# Revit family: xNBS_Bobrick_BackRest_B-5892
name_source: partatom
category: Furniture
revit_build: Autodesk Revit 2015 (Build: 20140606_1530(x64)
units: mm (PartAtom-declared; Revit-internal decimal feet)

## types (1)
- B-5892
    Assembly Code = C1030200
    AssetType = Fixed
    BIMObjectName = Bobrick_WCBackrests_B-5892
    BackRestDepth = 36 mm  [stored 0.11811 ft]
    BackRestMaterial = Foam-Bobrick-Polyurethane White
    BackRestWidth = 360 mm  [stored 1.1811 ft]
    Category = Pr_40_20_76_98:WC pan backrests
    Cost = 0 $
    Default Elevation = 680 mm  [stored 2.23097 ft]
    Depth = 242 mm  [stored 0.793963 ft]
    Description = 32mm (1-1⁄4") Diameter Stainless Steel Grab Bar with Padded Back Rest
    DurationUnit = year
    GrabBarRadius = 16 mm  [stored 0.0524934 ft]
    GrabRailMaterial = Stainless Steel-Bobrick-Type 308-18 Gauge-Satin
    Height = 32 mm  [stored 0.104987 ft]
    IfcExportAs = IfcFurnitureType
    IfcExportType = USERDEFINED
    Manufacturer = Bobrick Washroom Equipment Ltd.
    ManufacturerURL = http://www.bobrick.co.uk
    Model = B-5892
    ModelReference = WC Backrest
    NBSCertification = http://www.nationalbimlibrary.com
    NBSDescription = WC backrests
    NBSReference = 45-35-72/382
    Name = B-5892
    NominalDepth = 281 mm  [stored 0.921916 ft]
    NominalHeight = 160 mm  [stored 0.524934 ft]
    NominalLength = 405 mm
    NominalWidth = 405 mm
    ProductInformation = http://www.bobrick.co.uk
    Projection = 210 mm  [stored 0.688976 ft]
    Size = 405 x 281 x 160 mm
    URL = www.nationalbimlibrary.com
    Uniclass2015Code = Pr_40_20_76_98
    Uniclass2015Title = WC pan backrests
    Uniclass2015Version = Products v1.3
    Version = 1

note: [stored X ft] marks values corroborated as IEEE doubles in the binary element streams (Revit-internal decimal feet)

## geometry (parser evidence)
native form markers: Sweep x2
no freeform markers — native parametric forms only
